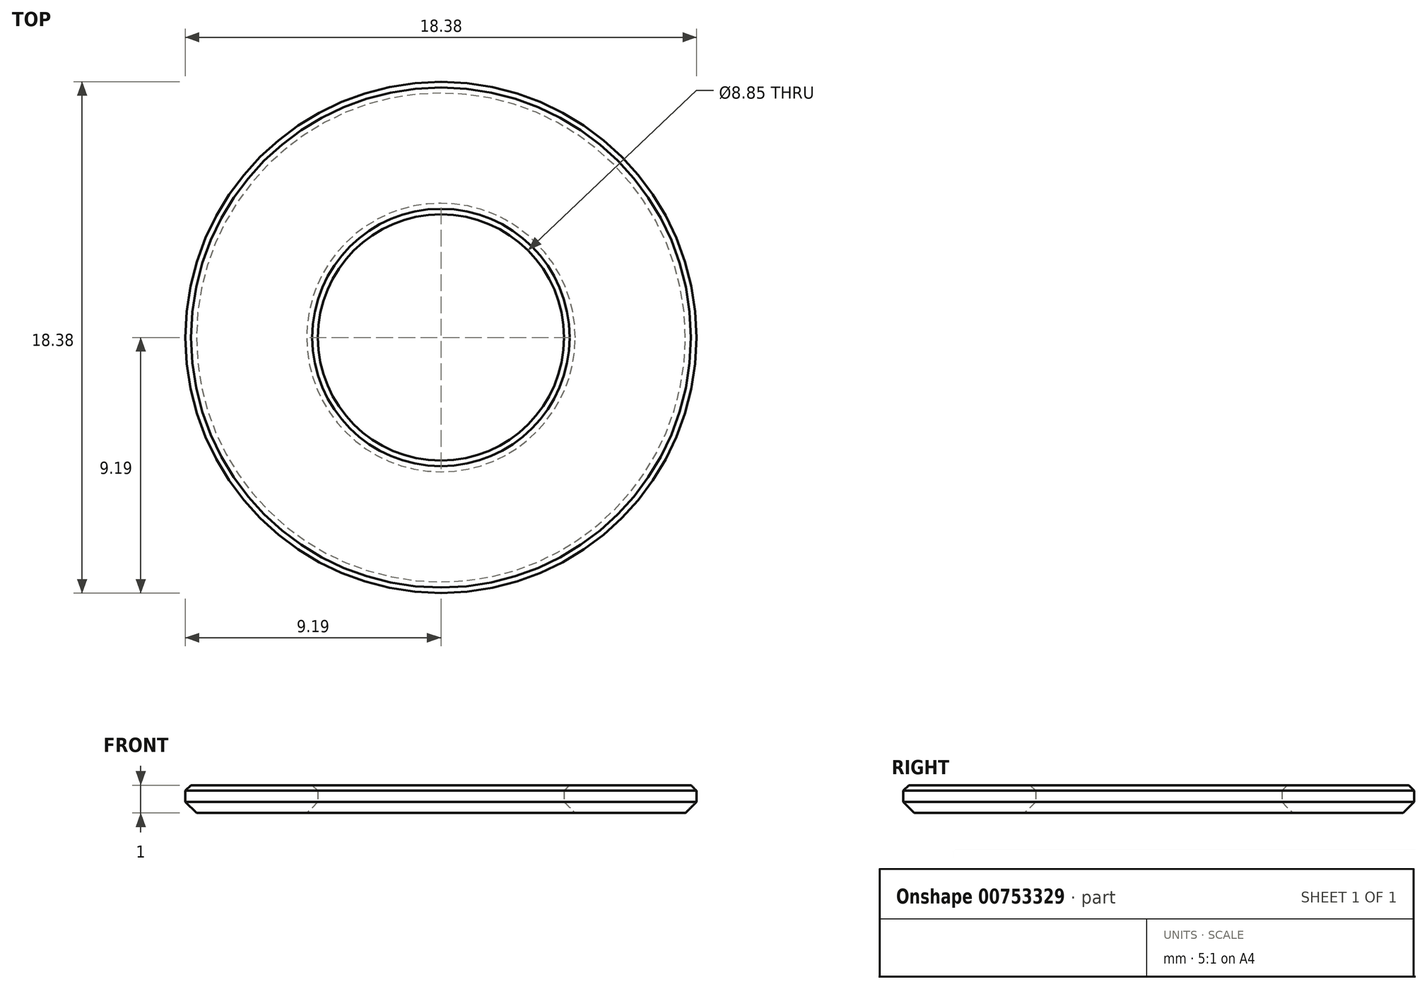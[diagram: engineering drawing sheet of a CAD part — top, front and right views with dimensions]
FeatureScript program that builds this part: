
annotation { "Feature Type Name" : "Feature", "Feature Type Description" : "" }
export const myFeature = defineFeature(function(context is Context, id is Id, definition is map)
    precondition{}
    {
        {
            assignVariable(context, id + "F0", {"name" : "Vol", "anyValue" : 1});
        }
        {
            var Q0;
            Q0=qCreatedBy(makeId("Top.planeOp"),FACE);
            var sketch = newSketch(context, id + "F1", { "sketchPlane" : qUnion([Q0])});
            skCircle(sketch, "E0", {"center": v(0, 0) * mm, "radius": 4.42 * mm});
            skCircle(sketch, "E1", {"center": v(0, 0) * mm, "radius": 9.19 * mm});
            skSolve(sketch);
        }
        {
            var Q0;
            Q0 = qSketchRegion(id + "F1", true);
            extrude(context, id + "F2", {"entities" : qUnion([Q0]), "depth" : (getVariable(context, 'Vol')) * mm, "offsetDistance" : 25 * mm});
        }
        {
            assignVariable(context, id + "F3", {"name" : "ChBas", "anyValue" : 0.4});
        }
        {
            assignVariable(context, id + "F4", {"name" : "ChHaut", "anyValue" : 0.2});
        }
        {
            var Q0;
            Q0=makeQuery(id+"F2.opExtrude","CAP_EDGE",EDGE,{"disambiguationData":[OSD([sQuery(id+"F1.wireOp",EDGE,"E1")])],"isStart":true});
            chamfer(context, id + "F5", {"entities" : qUnion([Q0]), "width" : (getVariable(context, 'ChBas')) * mm, "tangentPropagation" : true});
        }
        {
            var Q0;
            Q0=makeQuery(id+"F2.opExtrude","CAP_EDGE",EDGE,{"disambiguationData":[OSD([sQuery(id+"F1.wireOp",EDGE,"E1")])],"isStart":false});
            chamfer(context, id + "F6", {"entities" : qUnion([Q0]), "width" : getVariable(context, 'ChHaut') * mm, "tangentPropagation" : true});
        }
        {
            var Q0;
            Q0=makeQuery(id+"F2.opExtrude","CAP_EDGE",EDGE,{"disambiguationData":[OSD([sQuery(id+"F1.wireOp",EDGE,"E0")])],"isStart":true});
            chamfer(context, id + "F7", {"entities" : qUnion([Q0]), "width" : getVariable(context, 'ChBas') * mm, "tangentPropagation" : true});
        }
        {
            var Q0;
            Q0=makeQuery(id+"F2.opExtrude","CAP_EDGE",EDGE,{"disambiguationData":[OSD([sQuery(id+"F1.wireOp",EDGE,"E0")])],"isStart":false});
            chamfer(context, id + "F8", {"entities" : qUnion([Q0]), "width" : getVariable(context, 'ChHaut') * mm, "tangentPropagation" : true});
        }
    });
